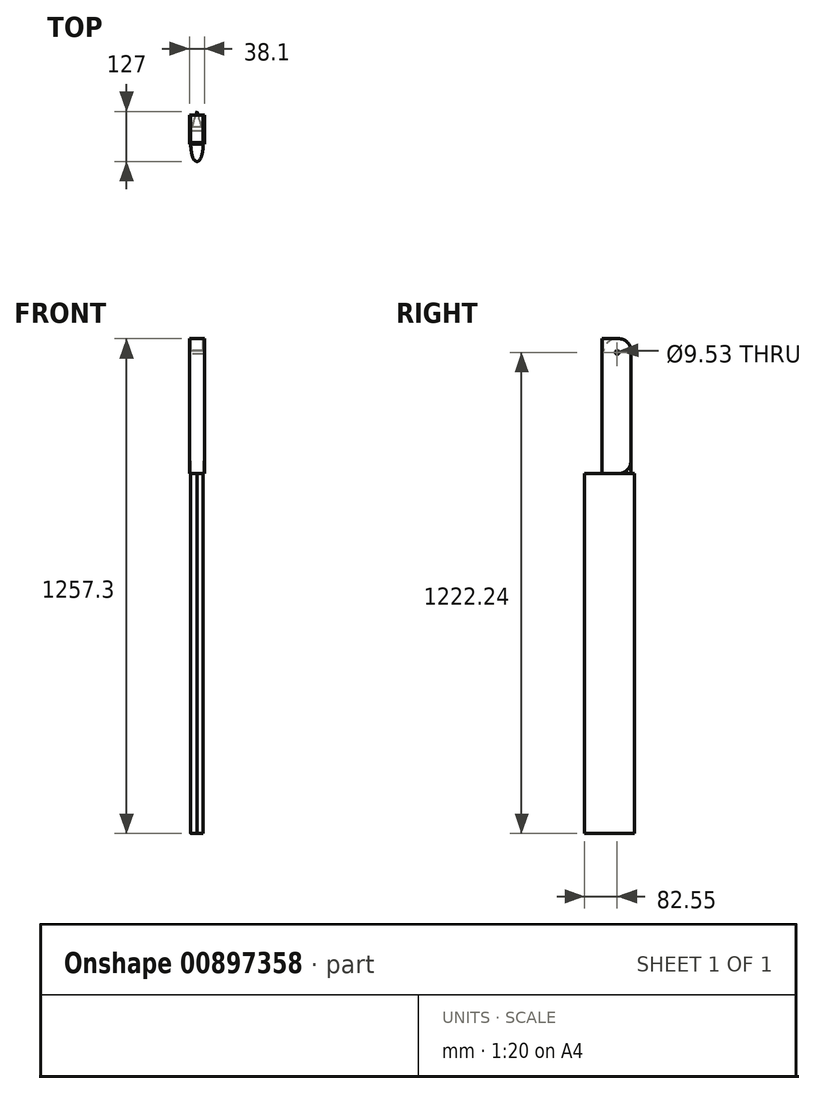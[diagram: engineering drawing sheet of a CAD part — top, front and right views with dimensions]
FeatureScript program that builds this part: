
annotation { "Feature Type Name" : "Feature", "Feature Type Description" : "" }
export const myFeature = defineFeature(function(context is Context, id is Id, definition is map)
    precondition{}
    {
        {
            var Q0;
            Q0=qCreatedBy(makeId("Top.planeOp"),FACE);
            var sketch = newSketch(context, id + "F0", { "sketchPlane" : qUnion([Q0])});
            skLineSegment(sketch, "E0.bottom", {"start": v(-19.05, 38.1) * mm, "end": v(19.05, 38.1) * mm});
            skLineSegment(sketch, "E0.top", {"start": v(-19.05, -38.1) * mm, "end": v(19.05, -38.1) * mm});
            skLineSegment(sketch, "E0.left", {"start": v(-19.05, 38.1) * mm, "end": v(-19.05, -38.1) * mm});
            skLineSegment(sketch, "E0.right", {"start": v(19.05, 38.1) * mm, "end": v(19.05, -38.1) * mm});
            skLineSegment(sketch, "E1.bottom", {"start": v(-15.88, 34.93) * mm, "end": v(15.87, 34.93) * mm});
            skLineSegment(sketch, "E1.top", {"start": v(-15.87, -34.93) * mm, "end": v(15.88, -34.93) * mm});
            skLineSegment(sketch, "E1.left", {"start": v(-15.88, 34.93) * mm, "end": v(-15.87, -34.93) * mm});
            skLineSegment(sketch, "E1.right", {"start": v(15.87, 34.93) * mm, "end": v(15.88, -34.93) * mm});
            skLineSegment(sketch, "E2", {"start": v(-15.88, 34.93) * mm, "end": v(-19.05, 34.93) * mm});
            skLineSegment(sketch, "E3", {"start": v(-19.05, 34.93) * mm, "end": v(15.87, 34.93) * mm});
            skLineSegment(sketch, "E4", {"start": v(15.87, 34.93) * mm, "end": v(19.05, 34.93) * mm});
            skSolve(sketch);
        }
        {
            var Q0;
            {var subQ1=sQuery(id+"F0.wireOp",EDGE,"E0.top");Q0=makeQuery(id+"F0.imprint","IMPRINT",FACE,{"disambiguationData":[TD([[makeQuery(id+"F0.imprint","IMPRINT",EDGE,{"derivedFrom":subQ1}),1.0]])]});}
            extrude(context, id + "F1", {"entities" : qUnion([Q0]), "oppositeDirection" : true, "depth" : 304.8 * mm, "offsetDistance" : 25.4 * mm, "hasSecondDirection" : true, "secondDirectionOppositeDirection" : false, "secondDirectionDepth" : 38.1 * mm});
        }
        {
            var Q0;
            Q0=makeQuery(id+"F1.opExtrude","CAP_EDGE",EDGE,{"disambiguationData":[OSD([sQuery(id+"F0.wireOp",EDGE,"E2")])],"isStart":true});
            var Q1;
            Q1=makeQuery(id+"F1.opExtrude","CAP_EDGE",EDGE,{"disambiguationData":[OSD([sQuery(id+"F0.wireOp",EDGE,"E4")])],"isStart":true});
            var Q2;
            Q2=makeQuery(id+"F1.opExtrude","CAP_EDGE",EDGE,{"disambiguationData":[OSD([sQuery(id+"F0.wireOp",EDGE,"E2")])],"isStart":false});
            var Q3;
            Q3=makeQuery(id+"F1.opExtrude","CAP_EDGE",EDGE,{"disambiguationData":[OSD([sQuery(id+"F0.wireOp",EDGE,"E4")])],"isStart":false});
            fillet(context, id + "F2", {"entities" : qUnion([Q0, Q1, Q2, Q3]), "radius" : 31.75 * mm, "tangentPropagation" : true, "defaultsChanged" : true, "vertexSettings" : [], "allowEdgeOverflow" : false});
        }
        {
            var Q0;
            Q0=makeQuery(id+"F1.opExtrude","SWEPT_FACE",FACE,{"disambiguationData":[OSD([sQuery(id+"F0.wireOp",EDGE,"E1.left")])]});
            var sketch = newSketch(context, id + "F3", { "sketchPlane" : qUnion([Q0])});
            skArc(sketch, "E5", {"start": v(34.93, 0) * mm, "mid": v(0, 38.1) * mm, "end": v(-34.93, 0) * mm});
            skLineSegment(sketch, "E6", {"start": v(-34.93, 38.1) * mm, "end": v(41.48, 38.1) * mm, "construction": true});
            skLineSegment(sketch, "E7", {"start": v(-34.93, -304.8) * mm, "end": v(34.93, -304.8) * mm});
            skLineSegment(sketch, "E8", {"start": v(34.93, -304.8) * mm, "end": v(34.93, -273.05) * mm});
            skCircle(sketch, "E9", {"center": v(0, 3.04) * mm, "radius": 4.76 * mm});
            skSolve(sketch);
        }
        {
            var Q0;
            Q0=makeQuery(id+"F3.imprint","IMPRINT",FACE,{"disambiguationData":[TD([[makeQuery(id+"F3.imprint","IMPRINT",EDGE,{"derivedFrom":sQuery(id+"F3.wireOp",EDGE,"E9")}),-1.0]])]});
            var Q1;
            {var subQ2=sQuery(id+"F3.wireOp",EDGE,"E8");Q1=makeQuery(id+"F3.imprint","IMPRINT",FACE,{"disambiguationData":[TD([[makeQuery(id+"F3.imprint","IMPRINT",EDGE,{"derivedFrom":subQ2}),1.0]])]});}
            var Q2;
            Q2=makeQuery(id+"F1.opExtrude","SWEPT_FACE",FACE,{"disambiguationData":[OSD([sQuery(id+"F0.wireOp",EDGE,"E1.right")])]});
            extrude(context, id + "F4", {"entities" : qUnion([Q0, Q1]), "endBound" : BoundingType.UP_TO_SURFACE, "depth" : 25.4 * mm, "endBoundEntityFace" : qUnion([Q2]), "offsetDistance" : 25.4 * mm});
        }
        {
            var Q0;
            Q0=makeQuery(id+"F4.opExtrude","SWEPT_FACE",FACE,{"disambiguationData":[OSD([sQuery(id+"F3.wireOp",EDGE,"E7")])]});
            var sketch = newSketch(context, id + "F5", { "sketchPlane" : qUnion([Q0])});
            skLineSegment(sketch, "E10", {"start": v(0, 82.55) * mm, "end": v(0, -44.45) * mm, "construction": true});
            skLineSegment(sketch, "E11", {"start": v(-26.7, 57.15) * mm, "end": v(34.24, 57.15) * mm, "construction": true});
            skFitSpline(sketch, "E12", {"points": [v(0, 82.55) * mm, v(15.88, 29.9) * mm, v(0, -44.45) * mm], "startDerivative": vector(78.97, 0.56) * mm, "endDerivative": vector(-46.65, -143.81) * mm});
            skFitSpline(sketch, "E13.MirrorCS", {"points": [v(0, 82.55) * mm, v(-15.87, 29.9) * mm, v(0, -44.45) * mm], "startDerivative": vector(-78.97, 0.56) * mm, "endDerivative": vector(46.65, -143.81) * mm});
            skSolve(sketch);
        }
        {
            var Q0;
            {var subQ0=sQuery(id+"F3.wireOp",EDGE,"E7");var subQ2=makeQuery(id+"F4.opExtrude","SWEPT_EDGE",EDGE,{"disambiguationData":[OSD([sQuery(id+"F0.wireOp",EDGE,"E1.top"),sQuery(id+"F0.wireOp",EDGE,"E1.left"),subQ0])]});Q0=makeQuery(id+"F5.imprint","IMPRINT",FACE,{"disambiguationData":[TD([[makeQuery(id+"F5.imprint","IMPRINT",EDGE,{"derivedFrom":subQ2}),-1.0]])]});}
            var Q1;
            {var subQ1=sQuery(id+"F3.wireOp",EDGE,"E7");var subQ8=makeQuery(id+"F4.opExtrude","SWEPT_EDGE",EDGE,{"disambiguationData":[OSD([sQuery(id+"F0.wireOp",EDGE,"E1.top"),sQuery(id+"F0.wireOp",EDGE,"E1.left"),subQ1])]});Q1=makeQuery(id+"F5.imprint","IMPRINT",FACE,{"disambiguationData":[TD([[makeQuery(id+"F5.imprint","IMPRINT",EDGE,{"derivedFrom":subQ8}),1.0]])]});}
            var Q2;
            {var subQ0=sQuery(id+"F5.wireOp",EDGE,"E13.MirrorCS");var subQ1=sQuery(id+"F5.wireOp",EDGE,"E12");var subQ2=makeQuery(id+"F5.imprint","INTERSECT",VERTEX,{"disambiguationData":[OD(1.0)],"derivedFrom":[subQ1,subQ0]});Q2=makeQuery(id+"F5.imprint","IMPRINT",FACE,{"disambiguationData":[TD([[makeQuery(id+"F5.imprint","IMPRINT",EDGE,{"disambiguationData":[TD([[subQ2,1.0]])],"derivedFrom":subQ1}),-1.0]])]});}
            extrude(context, id + "F6", {"entities" : qUnion([Q0, Q1, Q2]), "operationType" : NewBodyOperationType.ADD, "depth" : 914.4 * mm, "offsetDistance" : 25.4 * mm});
        }
        {
            var Q0;
            Q0=makeQuery(id+"F3.imprint","IMPRINT",FACE,{"disambiguationData":[TD([[makeQuery(id+"F3.imprint","IMPRINT",EDGE,{"derivedFrom":sQuery(id+"F3.wireOp",EDGE,"E9")}),1.0]])]});
            extrude(context, id + "F7", {"entities" : qUnion([Q0]), "operationType" : NewBodyOperationType.REMOVE, "endBound" : BoundingType.SYMMETRIC, "oppositeDirection" : true, "depth" : 101.6 * mm, "offsetDistance" : 25.4 * mm});
        }
    });
